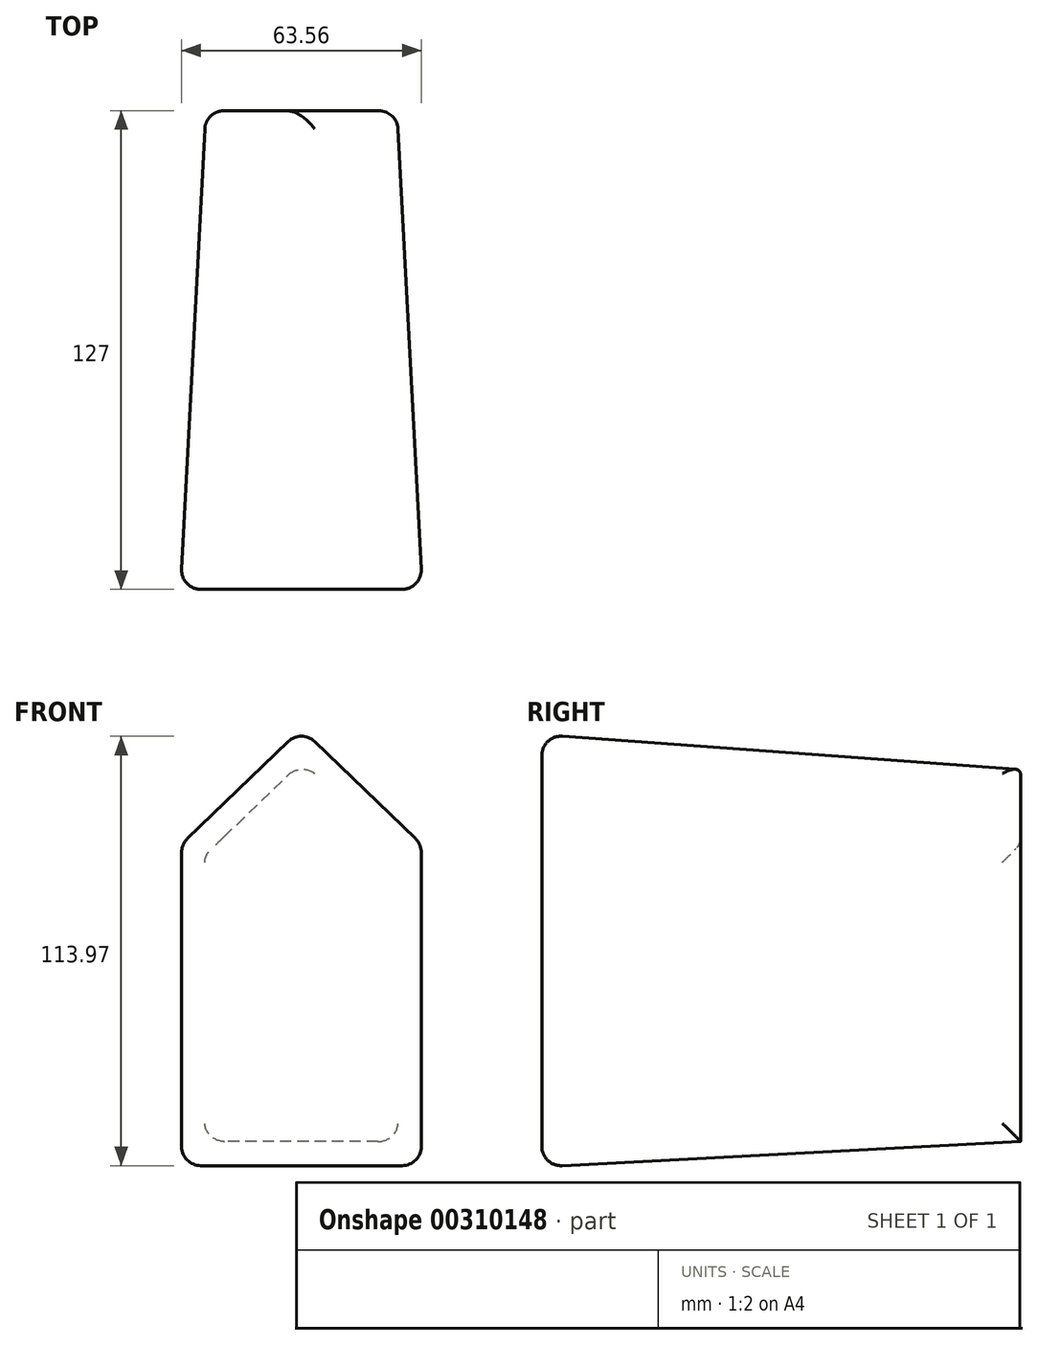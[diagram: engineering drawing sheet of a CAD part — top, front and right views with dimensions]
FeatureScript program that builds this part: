
annotation { "Feature Type Name" : "Feature", "Feature Type Description" : "" }
export const myFeature = defineFeature(function(context is Context, id is Id, definition is map)
    precondition{}
    {
        {
            var Q0;
            Q0=qCreatedBy(makeId("Front.planeOp"),FACE);
            var sketch = newSketch(context, id + "F0", { "sketchPlane" : qUnion([Q0])});
            skLineSegment(sketch, "E0.bottom", {"start": v(0, 0) * mm, "end": v(50.8, 0) * mm});
            skLineSegment(sketch, "E0.top", {"start": v(0, 76.2) * mm, "end": v(50.8, 76.2) * mm});
            skLineSegment(sketch, "E0.left", {"start": v(0, 0) * mm, "end": v(0, 76.2) * mm});
            skLineSegment(sketch, "E0.right", {"start": v(50.8, 0) * mm, "end": v(50.8, 76.2) * mm});
            skLineSegment(sketch, "E1", {"start": v(0, 76.2) * mm, "end": v(25.4, 100.7) * mm});
            skPoint(sketch, "E1.endSnap0", {"position": v(25.4, 76.2) * mm});
            skLineSegment(sketch, "E2", {"start": v(25.4, 100.7) * mm, "end": v(50.8, 76.2) * mm});
            skSolve(sketch);
        }
        {
            var Q0;
            Q0=makeQuery(id+"F0.imprint","IMPRINT",FACE,{"disambiguationData":[TD([[makeQuery(id+"F0.imprint","IMPRINT",EDGE,{"derivedFrom":sQuery(id+"F0.wireOp",EDGE,"E0.top")}),1.0]])]});
            var Q1;
            Q1=makeQuery(id+"F0.imprint","IMPRINT",FACE,{"disambiguationData":[TD([[makeQuery(id+"F0.imprint","IMPRINT",EDGE,{"derivedFrom":sQuery(id+"F0.wireOp",EDGE,"E0.bottom")}),1.0]])]});
            extrude(context, id + "F1", {"entities" : qUnion([Q0, Q1]), "depth" : 127 * mm, "hasDraft" : true, "draftAngle" : 3 * degree});
        }
        {
            var Q0;
            Q0=makeQuery(id+"F1.opExtrude","CAP_EDGE",EDGE,{"disambiguationData":[OSD([sQuery(id+"F0.wireOp",EDGE,"E2")])],"isStart":false});
            var Q1;
            Q1=makeQuery(id+"F1.opExtrude","SWEPT_EDGE",EDGE,{"disambiguationData":[OSD([sQuery(id+"F0.wireOp",EDGE,"E0.top"),sQuery(id+"F0.wireOp",EDGE,"E0.right"),sQuery(id+"F0.wireOp",EDGE,"E2")])]});
            var Q2;
            Q2=makeQuery(id+"F1.opExtrude","CAP_EDGE",EDGE,{"disambiguationData":[OSD([sQuery(id+"F0.wireOp",EDGE,"E0.right")])],"isStart":false});
            var Q3;
            Q3=makeQuery(id+"F1.opExtrude","CAP_EDGE",EDGE,{"disambiguationData":[OSD([sQuery(id+"F0.wireOp",EDGE,"E0.right")])],"isStart":true});
            var Q4;
            Q4=makeQuery(id+"F1.opExtrude","SWEPT_FACE",FACE,{"disambiguationData":[OSD([sQuery(id+"F0.wireOp",EDGE,"E2")])]});
            var Q5;
            Q5=makeQuery(id+"F1.opExtrude","SWEPT_FACE",FACE,{"disambiguationData":[OSD([sQuery(id+"F0.wireOp",EDGE,"E0.right")])]});
            var Q6;
            Q6=makeQuery(id+"F1.opExtrude","CAP_FACE",FACE,{"disambiguationData":[OSD([sQuery(id+"F0.wireOp",EDGE,"E0.bottom"),sQuery(id+"F0.wireOp",EDGE,"E0.left"),sQuery(id+"F0.wireOp",EDGE,"E0.right"),sQuery(id+"F0.wireOp",EDGE,"E1"),sQuery(id+"F0.wireOp",EDGE,"E2")])],"isStart":false});
            var Q7;
            Q7=makeQuery(id+"F1.opExtrude","SWEPT_FACE",FACE,{"disambiguationData":[OSD([sQuery(id+"F0.wireOp",EDGE,"E0.left")])]});
            fillet(context, id + "F2", {"entities" : qUnion([Q0, Q1, Q2, Q3, Q4, Q5, Q6, Q7]), "radius" : 5.08 * mm, "tangentPropagation" : true, "allowEdgeOverflow" : false});
        }
    });
